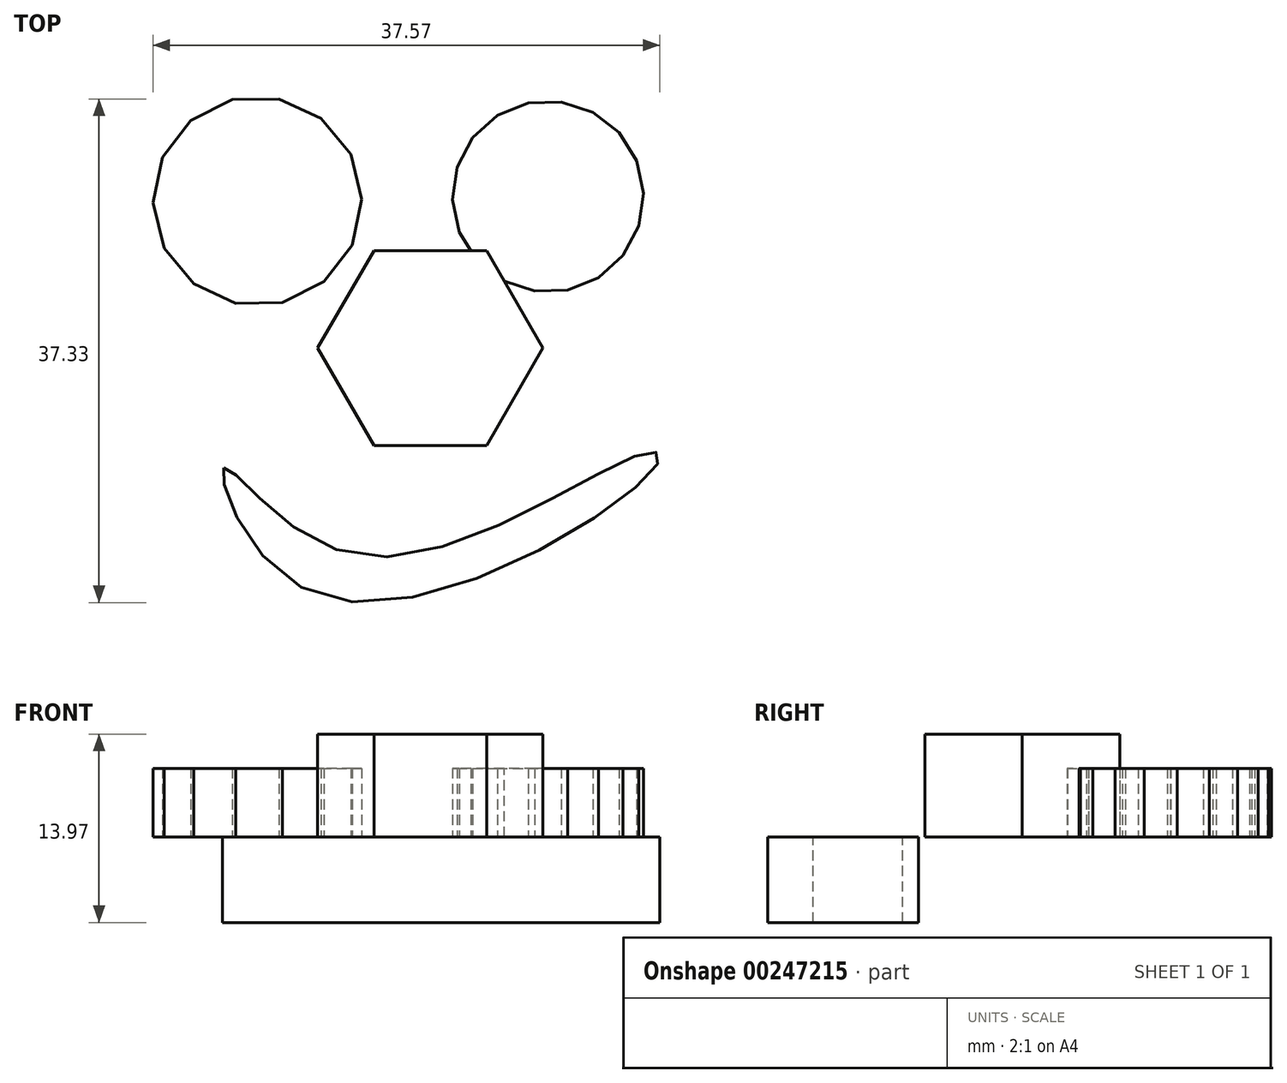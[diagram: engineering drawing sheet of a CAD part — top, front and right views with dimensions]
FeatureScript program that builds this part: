
annotation { "Feature Type Name" : "Feature", "Feature Type Description" : "" }
export const myFeature = defineFeature(function(context is Context, id is Id, definition is map)
    precondition{}
    {
        {
            var Q0;
            Q0=qCreatedBy(makeId("Top.planeOp"),FACE);
            var sketch = newSketch(context, id + "F0", { "sketchPlane" : qUnion([Q0])});
            skCircle(sketch, "E0.cCircle", {"center": v(-38.47, 35.22) * mm, "radius": 28.46 * mm, "construction": true});
            skLineSegment(sketch, "E0.0", {"start": v(-10, 41.72) * mm, "end": v(-10, 28.73) * mm});
            skLineSegment(sketch, "E0.1", {"start": v(-10, 28.73) * mm, "end": v(-15.65, 17.02) * mm});
            skLineSegment(sketch, "E0.2", {"start": v(-15.65, 17.02) * mm, "end": v(-25.8, 8.92) * mm});
            skLineSegment(sketch, "E0.3", {"start": v(-25.8, 8.92) * mm, "end": v(-38.47, 6.03) * mm});
            skLineSegment(sketch, "E0.4", {"start": v(-38.47, 6.03) * mm, "end": v(-51.14, 8.92) * mm});
            skLineSegment(sketch, "E0.5", {"start": v(-51.14, 8.92) * mm, "end": v(-61.3, 17.02) * mm});
            skLineSegment(sketch, "E0.6", {"start": v(-61.3, 17.02) * mm, "end": v(-66.93, 28.73) * mm});
            skLineSegment(sketch, "E0.7", {"start": v(-66.93, 28.73) * mm, "end": v(-66.93, 41.72) * mm});
            skLineSegment(sketch, "E0.8", {"start": v(-66.93, 41.72) * mm, "end": v(-61.3, 53.42) * mm});
            skLineSegment(sketch, "E0.9", {"start": v(-61.3, 53.42) * mm, "end": v(-51.14, 61.53) * mm});
            skLineSegment(sketch, "E0.10", {"start": v(-51.14, 61.53) * mm, "end": v(-38.47, 64.42) * mm});
            skLineSegment(sketch, "E0.11", {"start": v(-38.47, 64.42) * mm, "end": v(-25.8, 61.53) * mm});
            skLineSegment(sketch, "E0.12", {"start": v(-25.8, 61.53) * mm, "end": v(-15.65, 53.42) * mm});
            skLineSegment(sketch, "E0.13", {"start": v(-15.65, 53.42) * mm, "end": v(-10, 41.72) * mm});
            skPoint(sketch, "E0.0.midPoint", {"position": v(-10, 35.22) * mm});
            skSolve(sketch);
        }
        {
            var Q0;
            Q0=makeQuery(id+"F0.imprint","IMPRINT",FACE,{"disambiguationData":[TD([[makeQuery(id+"F0.imprint","IMPRINT",EDGE,{"derivedFrom":sQuery(id+"F0.wireOp",EDGE,"E0.0")}),-1.0]])]});
            var sketch = newSketch(context, id + "F1", { "sketchPlane" : qUnion([Q0])});
            skCircle(sketch, "E1.cCircle", {"center": v(-51, 45.58) * mm, "radius": 7.55 * mm, "construction": true});
            skLineSegment(sketch, "E1.0", {"start": v(-52.6, 38) * mm, "end": v(-55.74, 39.44) * mm});
            skLineSegment(sketch, "E1.1", {"start": v(-55.74, 39.44) * mm, "end": v(-57.93, 42.1) * mm});
            skLineSegment(sketch, "E1.2", {"start": v(-57.93, 42.1) * mm, "end": v(-58.75, 45.45) * mm});
            skLineSegment(sketch, "E1.3", {"start": v(-58.75, 45.45) * mm, "end": v(-58.04, 48.82) * mm});
            skLineSegment(sketch, "E1.4", {"start": v(-58.04, 48.82) * mm, "end": v(-55.94, 51.55) * mm});
            skLineSegment(sketch, "E1.5", {"start": v(-55.94, 51.55) * mm, "end": v(-52.86, 53.1) * mm});
            skLineSegment(sketch, "E1.6", {"start": v(-52.86, 53.1) * mm, "end": v(-49.41, 53.15) * mm});
            skLineSegment(sketch, "E1.7", {"start": v(-49.41, 53.15) * mm, "end": v(-46.28, 51.71) * mm});
            skLineSegment(sketch, "E1.8", {"start": v(-46.28, 51.71) * mm, "end": v(-44.09, 49.05) * mm});
            skLineSegment(sketch, "E1.9", {"start": v(-44.09, 49.05) * mm, "end": v(-43.27, 45.7) * mm});
            skLineSegment(sketch, "E1.10", {"start": v(-43.27, 45.7) * mm, "end": v(-43.98, 42.33) * mm});
            skLineSegment(sketch, "E1.11", {"start": v(-43.98, 42.33) * mm, "end": v(-46.08, 39.6) * mm});
            skLineSegment(sketch, "E1.12", {"start": v(-46.08, 39.6) * mm, "end": v(-49.16, 38.06) * mm});
            skLineSegment(sketch, "E1.13", {"start": v(-49.16, 38.06) * mm, "end": v(-52.6, 38) * mm});
            skPoint(sketch, "E1.0.midPoint", {"position": v(-54.17, 38.72) * mm});
            skSolve(sketch);
        }
        {
            var Q0;
            Q0 = qSketchRegion(id + "F1", true);
            extrude(context, id + "F2", {"entities" : qUnion([Q0]), "depth" : 5.08 * mm});
        }
        {
            var Q0;
            Q0=makeQuery(id+"F0.imprint","IMPRINT",FACE,{"disambiguationData":[TD([[makeQuery(id+"F0.imprint","IMPRINT",EDGE,{"derivedFrom":sQuery(id+"F0.wireOp",EDGE,"E0.0")}),-1.0]])]});
            var sketch = newSketch(context, id + "F3", { "sketchPlane" : qUnion([Q0])});
            skCircle(sketch, "E2.cCircle", {"center": v(-29.47, 45.92) * mm, "radius": 6.97 * mm, "construction": true});
            skLineSegment(sketch, "E2.0", {"start": v(-23.9, 41.56) * mm, "end": v(-25.72, 39.92) * mm});
            skLineSegment(sketch, "E2.1", {"start": v(-25.72, 39.92) * mm, "end": v(-28, 39) * mm});
            skLineSegment(sketch, "E2.2", {"start": v(-28, 39) * mm, "end": v(-30.46, 38.91) * mm});
            skLineSegment(sketch, "E2.3", {"start": v(-30.46, 38.91) * mm, "end": v(-32.8, 39.67) * mm});
            skLineSegment(sketch, "E2.4", {"start": v(-32.8, 39.67) * mm, "end": v(-34.74, 41.18) * mm});
            skLineSegment(sketch, "E2.5", {"start": v(-34.74, 41.18) * mm, "end": v(-36.04, 43.27) * mm});
            skLineSegment(sketch, "E2.6", {"start": v(-36.04, 43.27) * mm, "end": v(-36.55, 45.67) * mm});
            skLineSegment(sketch, "E2.7", {"start": v(-36.55, 45.67) * mm, "end": v(-36.2, 48.1) * mm});
            skLineSegment(sketch, "E2.8", {"start": v(-36.2, 48.1) * mm, "end": v(-35.05, 50.28) * mm});
            skLineSegment(sketch, "E2.9", {"start": v(-35.05, 50.28) * mm, "end": v(-33.22, 51.92) * mm});
            skLineSegment(sketch, "E2.10", {"start": v(-33.22, 51.92) * mm, "end": v(-30.94, 52.84) * mm});
            skLineSegment(sketch, "E2.11", {"start": v(-30.94, 52.84) * mm, "end": v(-28.49, 52.93) * mm});
            skLineSegment(sketch, "E2.12", {"start": v(-28.49, 52.93) * mm, "end": v(-26.15, 52.17) * mm});
            skLineSegment(sketch, "E2.13", {"start": v(-26.15, 52.17) * mm, "end": v(-24.21, 50.65) * mm});
            skLineSegment(sketch, "E2.14", {"start": v(-24.21, 50.65) * mm, "end": v(-22.91, 48.57) * mm});
            skLineSegment(sketch, "E2.15", {"start": v(-22.91, 48.57) * mm, "end": v(-22.4, 46.16) * mm});
            skLineSegment(sketch, "E2.16", {"start": v(-22.4, 46.16) * mm, "end": v(-22.74, 43.73) * mm});
            skLineSegment(sketch, "E2.17", {"start": v(-22.74, 43.73) * mm, "end": v(-23.9, 41.56) * mm});
            skPoint(sketch, "E2.0.midPoint", {"position": v(-24.81, 40.74) * mm});
            skSolve(sketch);
        }
        {
            var Q0;
            Q0 = qSketchRegion(id + "F3", true);
            extrude(context, id + "F4", {"entities" : qUnion([Q0]), "depth" : 5.08 * mm});
        }
        {
            var Q0;
            Q0=makeQuery(id+"F0.imprint","IMPRINT",FACE,{"disambiguationData":[TD([[makeQuery(id+"F0.imprint","IMPRINT",EDGE,{"derivedFrom":sQuery(id+"F0.wireOp",EDGE,"E0.0")}),-1.0]])]});
            var sketch = newSketch(context, id + "F5", { "sketchPlane" : qUnion([Q0])});
            skCircle(sketch, "E3.cCircle", {"center": v(-38.19, 34.68) * mm, "radius": 7.23 * mm, "construction": true});
            skLineSegment(sketch, "E3.0", {"start": v(-34.02, 27.46) * mm, "end": v(-42.36, 27.46) * mm});
            skLineSegment(sketch, "E3.1", {"start": v(-42.36, 27.46) * mm, "end": v(-46.53, 34.68) * mm});
            skLineSegment(sketch, "E3.2", {"start": v(-46.53, 34.68) * mm, "end": v(-42.36, 41.91) * mm});
            skLineSegment(sketch, "E3.3", {"start": v(-42.36, 41.91) * mm, "end": v(-34.02, 41.91) * mm});
            skLineSegment(sketch, "E3.4", {"start": v(-34.02, 41.91) * mm, "end": v(-29.84, 34.68) * mm});
            skLineSegment(sketch, "E3.5", {"start": v(-29.84, 34.68) * mm, "end": v(-34.02, 27.46) * mm});
            skPoint(sketch, "E3.0.midPoint", {"position": v(-38.19, 27.46) * mm});
            skSolve(sketch);
        }
        {
            var Q0;
            Q0 = qSketchRegion(id + "F5", true);
            extrude(context, id + "F6", {"entities" : qUnion([Q0]), "operationType" : NewBodyOperationType.ADD, "depth" : 7.62 * mm});
        }
        {
            var Q0;
            Q0=makeQuery(id+"F6.opExtrude","CAP_FACE",FACE,{"disambiguationData":[OSD([sQuery(id+"F5.wireOp",EDGE,"E3.0"),sQuery(id+"F5.wireOp",EDGE,"E3.1"),sQuery(id+"F5.wireOp",EDGE,"E3.2"),sQuery(id+"F5.wireOp",EDGE,"E3.3"),sQuery(id+"F5.wireOp",EDGE,"E3.4"),sQuery(id+"F5.wireOp",EDGE,"E3.5")])],"isStart":false});
            var sketch = newSketch(context, id + "F7", { "sketchPlane" : qUnion([Q0])});
            skCircle(sketch, "E4.cCircle", {"center": v(-40.43, 32) * mm, "radius": 2.54 * mm, "construction": true});
            skLineSegment(sketch, "E4.0", {"start": v(-38.03, 31.06) * mm, "end": v(-38.41, 30.4) * mm});
            skLineSegment(sketch, "E4.1", {"start": v(-38.41, 30.4) * mm, "end": v(-38.98, 29.88) * mm});
            skLineSegment(sketch, "E4.2", {"start": v(-38.98, 29.88) * mm, "end": v(-39.67, 29.55) * mm});
            skLineSegment(sketch, "E4.3", {"start": v(-39.67, 29.55) * mm, "end": v(-40.43, 29.43) * mm});
            skLineSegment(sketch, "E4.4", {"start": v(-40.43, 29.43) * mm, "end": v(-41.18, 29.55) * mm});
            skLineSegment(sketch, "E4.5", {"start": v(-41.18, 29.55) * mm, "end": v(-41.88, 29.88) * mm});
            skLineSegment(sketch, "E4.6", {"start": v(-41.88, 29.88) * mm, "end": v(-42.44, 30.4) * mm});
            skLineSegment(sketch, "E4.7", {"start": v(-42.44, 30.4) * mm, "end": v(-42.82, 31.06) * mm});
            skLineSegment(sketch, "E4.8", {"start": v(-42.82, 31.06) * mm, "end": v(-43, 31.81) * mm});
            skLineSegment(sketch, "E4.9", {"start": v(-43, 31.81) * mm, "end": v(-42.93, 32.58) * mm});
            skLineSegment(sketch, "E4.10", {"start": v(-42.93, 32.58) * mm, "end": v(-42.65, 33.3) * mm});
            skLineSegment(sketch, "E4.11", {"start": v(-42.65, 33.3) * mm, "end": v(-42.18, 33.9) * mm});
            skLineSegment(sketch, "E4.12", {"start": v(-42.18, 33.9) * mm, "end": v(-41.54, 34.32) * mm});
            skLineSegment(sketch, "E4.13", {"start": v(-41.54, 34.32) * mm, "end": v(-40.8, 34.55) * mm});
            skLineSegment(sketch, "E4.14", {"start": v(-40.8, 34.55) * mm, "end": v(-40.04, 34.55) * mm});
            skLineSegment(sketch, "E4.15", {"start": v(-40.04, 34.55) * mm, "end": v(-39.3, 34.32) * mm});
            skLineSegment(sketch, "E4.16", {"start": v(-39.3, 34.32) * mm, "end": v(-38.68, 33.9) * mm});
            skLineSegment(sketch, "E4.17", {"start": v(-38.68, 33.9) * mm, "end": v(-38.2, 33.3) * mm});
            skLineSegment(sketch, "E4.18", {"start": v(-38.2, 33.3) * mm, "end": v(-37.92, 32.58) * mm});
            skLineSegment(sketch, "E4.19", {"start": v(-37.92, 32.58) * mm, "end": v(-37.86, 31.81) * mm});
            skLineSegment(sketch, "E4.20", {"start": v(-37.86, 31.81) * mm, "end": v(-38.03, 31.06) * mm});
            skPoint(sketch, "E4.0.midPoint", {"position": v(-38.22, 30.73) * mm});
            skSolve(sketch);
        }
        {
            var Q0;
            Q0 = qSketchRegion(id + "F7", true);
            extrude(context, id + "F8", {"entities" : qUnion([Q0]), "operationType" : NewBodyOperationType.ADD, "oppositeDirection" : true, "depth" : 2.54 * mm});
        }
        {
            var Q0;
            Q0=makeQuery(id+"F6.opExtrude","CAP_FACE",FACE,{"disambiguationData":[OSD([sQuery(id+"F5.wireOp",EDGE,"E3.0"),sQuery(id+"F5.wireOp",EDGE,"E3.1"),sQuery(id+"F5.wireOp",EDGE,"E3.2"),sQuery(id+"F5.wireOp",EDGE,"E3.3"),sQuery(id+"F5.wireOp",EDGE,"E3.4"),sQuery(id+"F5.wireOp",EDGE,"E3.5")])],"isStart":false});
            var sketch = newSketch(context, id + "F9", { "sketchPlane" : qUnion([Q0])});
            skCircle(sketch, "E5.cCircle", {"center": v(-41.12, 32.7) * mm, "radius": 2.19 * mm, "construction": true});
            skLineSegment(sketch, "E5.0", {"start": v(-40.82, 30.52) * mm, "end": v(-41.42, 30.52) * mm});
            skLineSegment(sketch, "E5.1", {"start": v(-41.42, 30.52) * mm, "end": v(-42, 30.68) * mm});
            skLineSegment(sketch, "E5.2", {"start": v(-42, 30.68) * mm, "end": v(-42.51, 31) * mm});
            skLineSegment(sketch, "E5.3", {"start": v(-42.51, 31) * mm, "end": v(-42.92, 31.44) * mm});
            skLineSegment(sketch, "E5.4", {"start": v(-42.92, 31.44) * mm, "end": v(-43.2, 31.97) * mm});
            skLineSegment(sketch, "E5.5", {"start": v(-43.2, 31.97) * mm, "end": v(-43.32, 32.56) * mm});
            skLineSegment(sketch, "E5.6", {"start": v(-43.32, 32.56) * mm, "end": v(-43.28, 33.16) * mm});
            skLineSegment(sketch, "E5.7", {"start": v(-43.28, 33.16) * mm, "end": v(-43.08, 33.72) * mm});
            skLineSegment(sketch, "E5.8", {"start": v(-43.08, 33.72) * mm, "end": v(-42.73, 34.22) * mm});
            skLineSegment(sketch, "E5.9", {"start": v(-42.73, 34.22) * mm, "end": v(-42.27, 34.6) * mm});
            skLineSegment(sketch, "E5.10", {"start": v(-42.27, 34.6) * mm, "end": v(-41.71, 34.83) * mm});
            skLineSegment(sketch, "E5.11", {"start": v(-41.71, 34.83) * mm, "end": v(-41.12, 34.92) * mm});
            skLineSegment(sketch, "E5.12", {"start": v(-41.12, 34.92) * mm, "end": v(-40.52, 34.83) * mm});
            skLineSegment(sketch, "E5.13", {"start": v(-40.52, 34.83) * mm, "end": v(-39.97, 34.6) * mm});
            skLineSegment(sketch, "E5.14", {"start": v(-39.97, 34.6) * mm, "end": v(-39.5, 34.22) * mm});
            skLineSegment(sketch, "E5.15", {"start": v(-39.5, 34.22) * mm, "end": v(-39.16, 33.72) * mm});
            skLineSegment(sketch, "E5.16", {"start": v(-39.16, 33.72) * mm, "end": v(-38.96, 33.16) * mm});
            skLineSegment(sketch, "E5.17", {"start": v(-38.96, 33.16) * mm, "end": v(-38.92, 32.56) * mm});
            skLineSegment(sketch, "E5.18", {"start": v(-38.92, 32.56) * mm, "end": v(-39.04, 31.97) * mm});
            skLineSegment(sketch, "E5.19", {"start": v(-39.04, 31.97) * mm, "end": v(-39.31, 31.44) * mm});
            skLineSegment(sketch, "E5.20", {"start": v(-39.31, 31.44) * mm, "end": v(-39.73, 31) * mm});
            skLineSegment(sketch, "E5.21", {"start": v(-39.73, 31) * mm, "end": v(-40.24, 30.68) * mm});
            skLineSegment(sketch, "E5.22", {"start": v(-40.24, 30.68) * mm, "end": v(-40.82, 30.52) * mm});
            skPoint(sketch, "E5.0.midPoint", {"position": v(-41.12, 30.52) * mm});
            skSolve(sketch);
        }
        {
            var Q0;
            Q0 = qSketchRegion(id + "F9", true);
            extrude(context, id + "F10", {"entities" : qUnion([Q0]), "operationType" : NewBodyOperationType.ADD, "oppositeDirection" : true, "depth" : 2.54 * mm});
        }
        {
            var Q0;
            Q0=makeQuery(id+"F0.imprint","IMPRINT",FACE,{"disambiguationData":[TD([[makeQuery(id+"F0.imprint","IMPRINT",EDGE,{"derivedFrom":sQuery(id+"F0.wireOp",EDGE,"E0.0")}),-1.0]])]});
            var sketch = newSketch(context, id + "F11", { "sketchPlane" : qUnion([Q0])});
            skFitSpline(sketch, "E6", {"points": [v(-53.5, 25.8) * mm, v(-46.1, 16.24) * mm, v(-21.26, 26.27) * mm, v(-21.97, 26.99) * mm, v(-43.7, 19.35) * mm, v(-53.5, 25.8) * mm]});
            skSolve(sketch);
        }
        {
            var Q0;
            Q0 = qSketchRegion(id + "F11", true);
            extrude(context, id + "F12", {"entities" : qUnion([Q0]), "oppositeDirection" : true, "depth" : 6.35 * mm});
        }
    });
